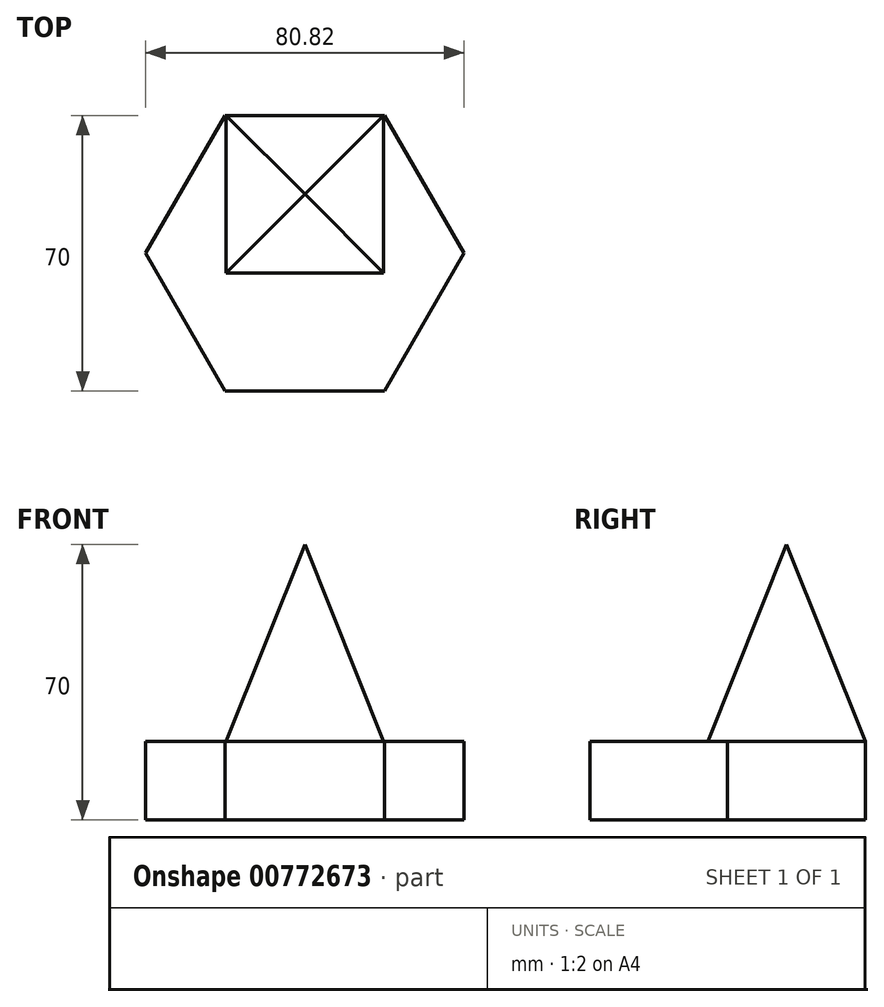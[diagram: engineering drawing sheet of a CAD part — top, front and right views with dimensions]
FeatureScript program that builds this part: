
annotation { "Feature Type Name" : "Feature", "Feature Type Description" : "" }
export const myFeature = defineFeature(function(context is Context, id is Id, definition is map)
    precondition{}
    {
        {
            var Q0;
            Q0=qCreatedBy(makeId("Top.planeOp"),FACE);
            var sketch = newSketch(context, id + "F0", { "sketchPlane" : qUnion([Q0])});
            skLineSegment(sketch, "E0", {"start": v(0, 0) * mm, "end": v(50, 0) * mm});
            skLineSegment(sketch, "E1", {"start": v(50, 0) * mm, "end": v(50, -35) * mm});
            skLineSegment(sketch, "E2.0", {"start": v(29.8, 0) * mm, "end": v(70.2, 0) * mm});
            skLineSegment(sketch, "E2.1", {"start": v(70.2, 0) * mm, "end": v(90.41, -35) * mm});
            skLineSegment(sketch, "E2.2", {"start": v(90.41, -35) * mm, "end": v(70.2, -70) * mm});
            skLineSegment(sketch, "E2.3", {"start": v(70.2, -70) * mm, "end": v(29.8, -70) * mm});
            skLineSegment(sketch, "E2.4", {"start": v(29.8, -70) * mm, "end": v(9.59, -35) * mm});
            skLineSegment(sketch, "E2.5", {"start": v(9.59, -35) * mm, "end": v(29.8, 0) * mm});
            skLineSegment(sketch, "E3", {"start": v(50, 0) * mm, "end": v(50, -20) * mm});
            skLineSegment(sketch, "E4.0", {"start": v(30, -40) * mm, "end": v(30, 0) * mm});
            skLineSegment(sketch, "E4.1", {"start": v(30, 0) * mm, "end": v(70, 0) * mm});
            skLineSegment(sketch, "E4.2", {"start": v(70, 0) * mm, "end": v(70, -40) * mm});
            skLineSegment(sketch, "E4.3", {"start": v(70, -40) * mm, "end": v(30, -40) * mm});
            skSolve(sketch);
        }
        {
            var Q0;
            {var subQ4=sQuery(id+"F0.wireOp",EDGE,"E4.0");Q0=makeQuery(id+"F0.imprint","IMPRINT",FACE,{"disambiguationData":[TD([[makeQuery(id+"F0.imprint","IMPRINT",EDGE,{"derivedFrom":subQ4}),-1.0]])]});}
            extrude(context, id + "F1", {"entities" : qUnion([Q0]), "depth" : 20 * mm, "offsetDistance" : 25 * mm});
        }
        {
            var Q0;
            Q0=qCreatedBy(makeId("Top.planeOp"),FACE);
            cPlane(context, id + "F2", {"entities" : qUnion([Q0]), "cplaneType" : CPlaneType.OFFSET, "offset" : 70 * mm, "width" : 150 * mm, "height" : 150 * mm});
        }
        {
            var Q0;
            Q0=qCreatedBy(id+"F2.planeOp",FACE);
            var sketch = newSketch(context, id + "F3", { "sketchPlane" : qUnion([Q0])});
            skPoint(sketch, "E5.0", {"position": v(50, -20) * mm});
            skSolve(sketch);
        }
        {
            var Q1;
            Q1=makeQuery(id+"F1.opExtrude","CAP_FACE",FACE,{"disambiguationData":[OSD([sQuery(id+"F0.wireOp",EDGE,"E4.0"),sQuery(id+"F0.wireOp",EDGE,"E4.1"),sQuery(id+"F0.wireOp",EDGE,"E4.2"),sQuery(id+"F0.wireOp",EDGE,"E4.3")])],"isStart":false});
            var Q2;
            Q2=sQuery(id+"F3.wireOp",VERTEX,"E5.0");
            loft(context, id + "F4", {"operationType" : NewBodyOperationType.ADD, "sheetProfilesArray" : [{ "sheetProfileEntities" : qUnion([Q1]) }, { "sheetProfileEntities" : qUnion([Q2]) }]});
        }
        {
            var Q0;
            {var subQ0=sQuery(id+"F0.wireOp",EDGE,"E2.1");Q0=makeQuery(id+"F0.imprint","IMPRINT",FACE,{"disambiguationData":[TD([[makeQuery(id+"F0.imprint","IMPRINT",EDGE,{"derivedFrom":subQ0}),-1.0]])]});}
            extrude(context, id + "F5", {"entities" : qUnion([Q0]), "operationType" : NewBodyOperationType.ADD, "depth" : 20 * mm, "offsetDistance" : 25 * mm});
        }
    });
